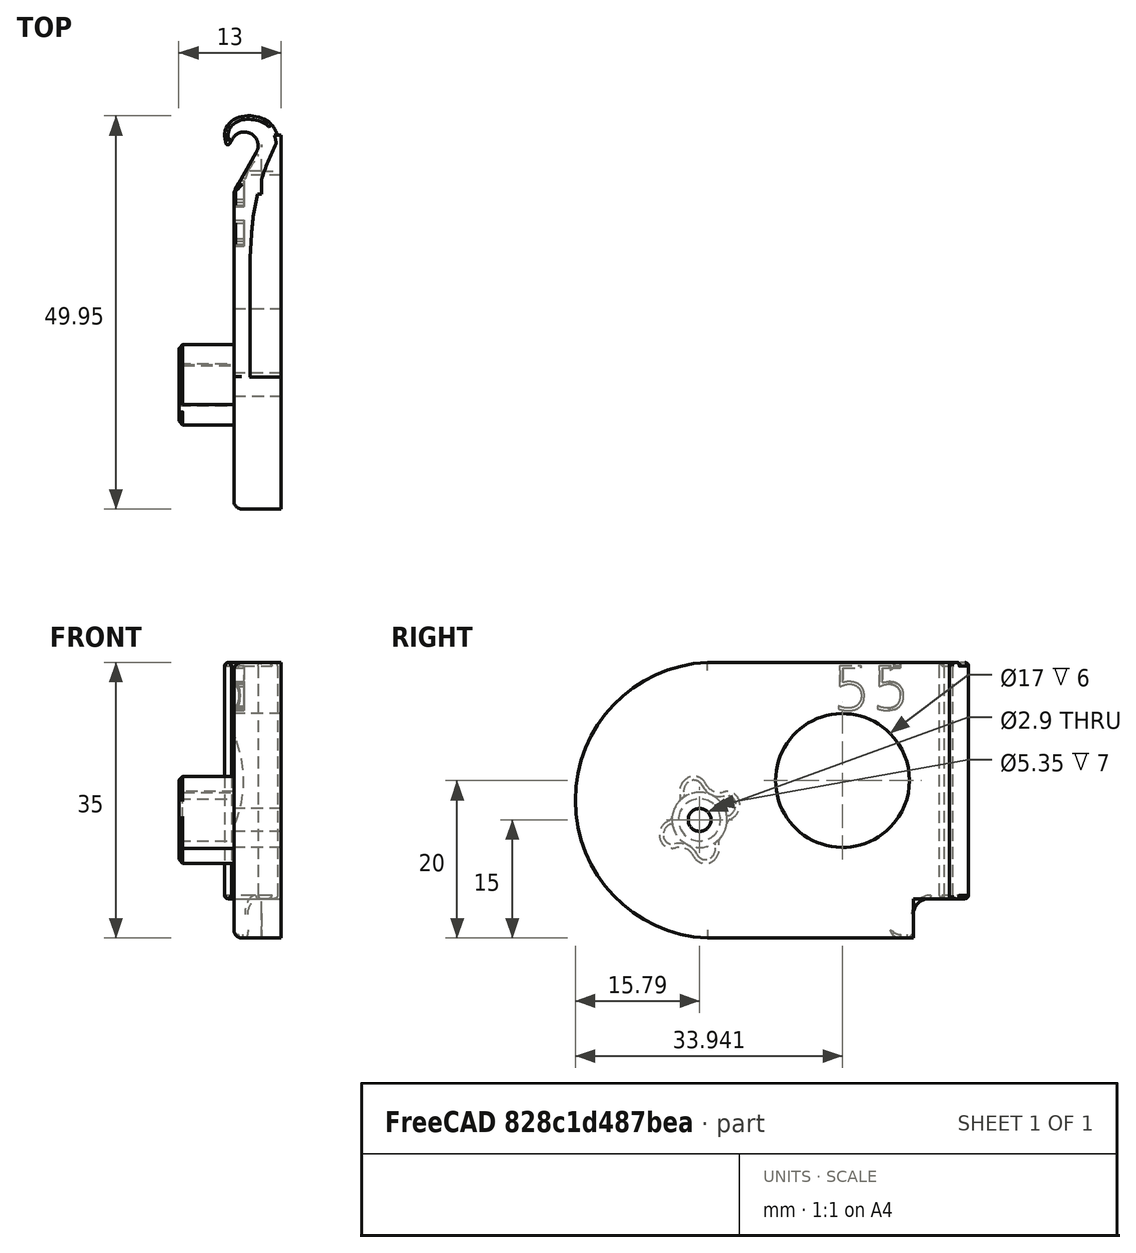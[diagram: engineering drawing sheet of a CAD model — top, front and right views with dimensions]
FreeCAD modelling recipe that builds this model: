
FCSTD DOCUMENT  (FreeCAD 0.18R)
Label: hinge-right-155deg-flat
License: All rights reserved
LicenseURL: http://en.wikipedia.org/wiki/All_rights_reserved
objects: App::FeaturePython×4, Part::FeaturePython×2, Part::Part2DObjectPython×1, Part::Extrusion×1, Part::Cut×1
note: 5 computed .brp shape members not serialized (recipe doc carries the construction recipe); baked Part::Feature solids carry a one-line shape summary decoded from their .brp

FEATURE [Part::FeaturePython] pillar_base_001  label="pillar-base_001"  # a2plus imported part (geometry in sourceFile) (typed FeaturePython)
  Placement = pos=(0.000602273,-56.4392,26.312) rot=(-1,0,0;0.87249rad)
  a2p_Version = V0.1
  fixedPosition = false
  objectType = a2pPart
  sourceFile = ./parts/pillar-base.fcstd
  subassemblyImport = false
  timeLastImport = 1.60452e+09
  updateColors = true
FEATURE [Part::Part2DObjectPython] ShapeString  # Draft 2D object (typed FeaturePython)
  FontFile = <path>
  Placement = pos=(1.61,10.5,29) rot=(0.57735,-0.57735,-0.57735;2.0944rad)
  Size = 6
  String = 55
  Tracking = 0
FEATURE [Part::Extrusion] Extrude
  Base = -> ShapeString
  Dir = (-1,0,0)
  DirMode = 2
  FaceMakerClass = Part::FaceMakerBullseye
  LengthFwd = 3.5
  LengthRev = 0
  Placement = pos=(0,0,0) rot=(0,0,1;3.14159rad)
  Solid = false
  Symmetric = false
FEATURE [Part::FeaturePython] bracket_right_flat_001  label="bracket-right-flat_001"  # a2plus imported part (geometry in sourceFile) (typed FeaturePython)
  Placement = pos=(0,0,0) rot=(0,0,1;3.14159rad)
  a2p_Version = V0.1
  fixedPosition = true
  objectType = a2pPart
  sourceFile = ./parts/bracket-right-flat.fcstd
  subassemblyImport = false
  timeLastImport = 1.60489e+09
  updateColors = true
FEATURE [App::FeaturePython] axisCoincident_001  label="axisCoincident_001__bracket-right-flat_001"  # a2plus constraint (typed FeaturePython)
  Object1 = pillar_base_001
  Object2 = bracket_right_flat_001
  ParentTreeObject = -> pillar_base_001
  SubElement1 = Face17
  SubElement2 = Face31
  Suppressed = false
  Type = axial
  directionConstraint = 1
  lockRotation = false
FEATURE [App::FeaturePython] axisCoincident_001_mirror  label="axisCoincident_001__pillar-base_001"  # a2plus constraint (typed FeaturePython)
  Object1 = pillar_base_001
  Object2 = bracket_right_flat_001
  ParentTreeObject = -> bracket_right_flat_001
  SubElement1 = Face17
  SubElement2 = Face31
  Suppressed = false
  Type = axial
  directionConstraint = 1
  lockRotation = false
FEATURE [App::FeaturePython] planeCoincident_001  label="planeCoincident_001__bracket-right-flat_001"  # a2plus constraint (typed FeaturePython)
  Object1 = pillar_base_001
  Object2 = bracket_right_flat_001
  ParentTreeObject = -> pillar_base_001
  SubElement1 = Face1
  SubElement2 = Face57
  Suppressed = false
  Type = plane
  directionConstraint = 1
  offset = 0
FEATURE [App::FeaturePython] planeCoincident_001_mirror  label="planeCoincident_001__pillar-base_001"  # a2plus constraint (typed FeaturePython)
  Object1 = pillar_base_001
  Object2 = bracket_right_flat_001
  ParentTreeObject = -> bracket_right_flat_001
  SubElement1 = Face1
  SubElement2 = Face57
  Suppressed = false
  Type = plane
  directionConstraint = 1
  offset = 0
FEATURE [Part::Cut] Cut
  Base = -> bracket_right_flat_001
  Tool = -> Extrude
note: 1 file-system path scrubbed to <path> (originals preserved in the JSON sidecar)
